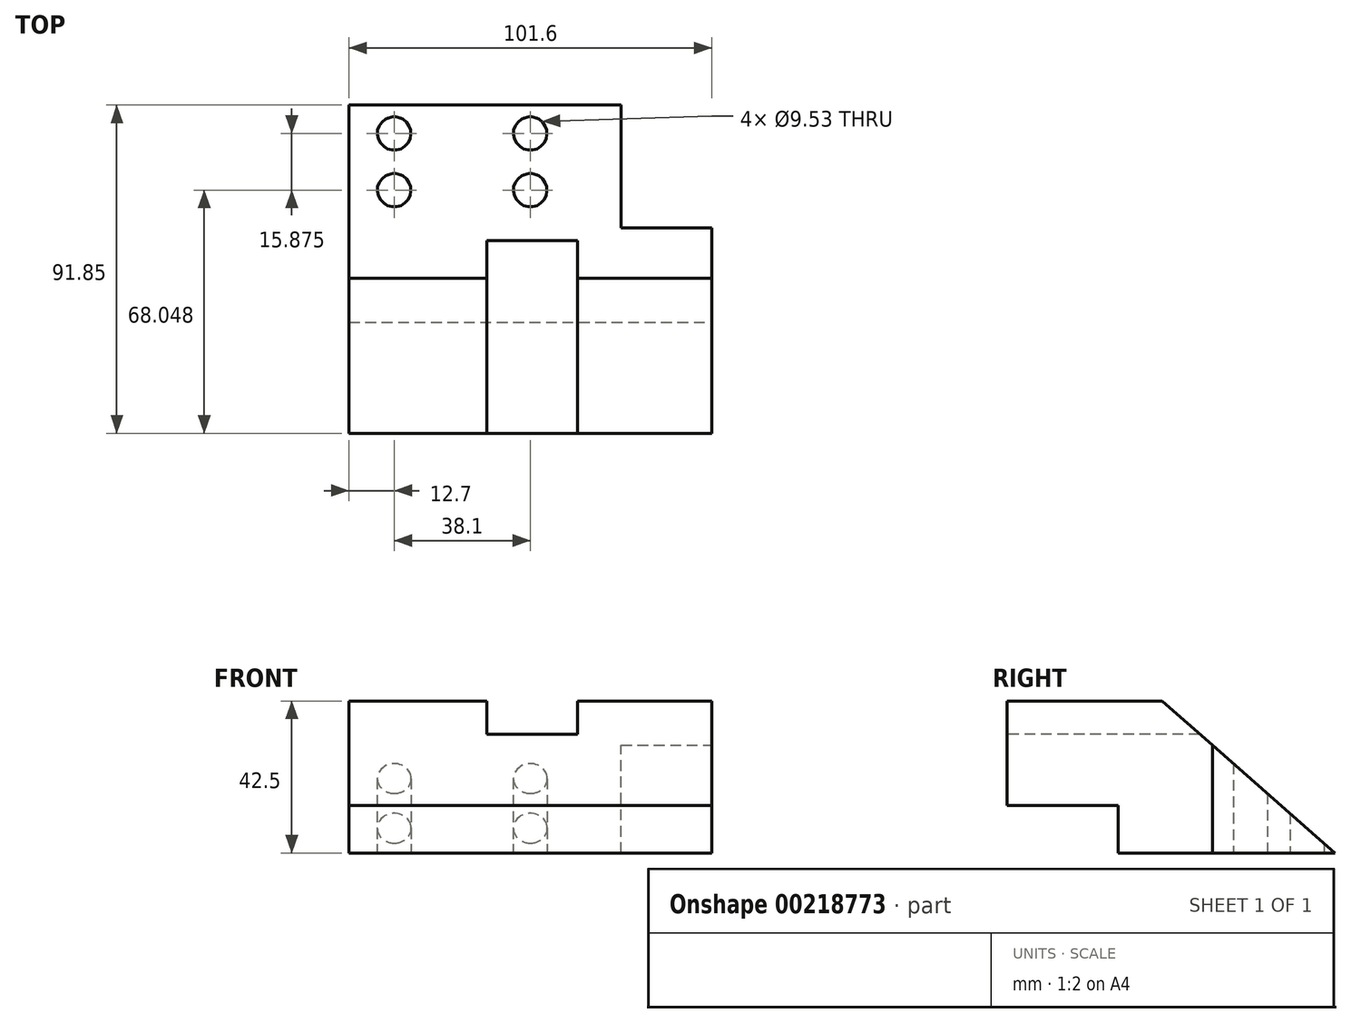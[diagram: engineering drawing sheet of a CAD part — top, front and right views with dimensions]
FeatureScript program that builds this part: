
annotation { "Feature Type Name" : "Feature", "Feature Type Description" : "" }
export const myFeature = defineFeature(function(context is Context, id is Id, definition is map)
    precondition{}
    {
        {
            var Q0;
            Q0=qCreatedBy(makeId("Right.planeOp"),FACE);
            var sketch = newSketch(context, id + "F0", { "sketchPlane" : qUnion([Q0])});
            skLineSegment(sketch, "E0", {"start": v(0, 0) * mm, "end": v(0, 29.24) * mm});
            skLineSegment(sketch, "E1", {"start": v(0, 29.24) * mm, "end": v(43.36, 29.24) * mm});
            skLineSegment(sketch, "E2", {"start": v(43.36, 29.24) * mm, "end": v(91.85, -13.26) * mm});
            skLineSegment(sketch, "E3", {"start": v(91.85, -13.26) * mm, "end": v(31.1, -13.26) * mm});
            skLineSegment(sketch, "E4", {"start": v(31.1, -13.26) * mm, "end": v(31.1, 0) * mm});
            skLineSegment(sketch, "E5", {"start": v(31.1, 0) * mm, "end": v(0, 0) * mm});
            skSolve(sketch);
        }
        {
            var Q0;
            Q0 = qSketchRegion(id + "F0", true);
            extrude(context, id + "F1", {"entities" : qUnion([Q0]), "endBound" : BoundingType.SYMMETRIC, "oppositeDirection" : true, "depth" : 101.6 * mm});
        }
        {
            var Q0;
            Q0=makeQuery(id+"F1.opExtrude","SWEPT_FACE",FACE,{"disambiguationData":[OSD([sQuery(id+"F0.wireOp",EDGE,"E0")])]});
            var sketch = newSketch(context, id + "F2", { "sketchPlane" : qUnion([Q0])});
            skLineSegment(sketch, "E6", {"start": v(0, 29.24) * mm, "end": v(-12.24, 29.24) * mm});
            skLineSegment(sketch, "E7", {"start": v(-12.24, 29.24) * mm, "end": v(-12.24, 20.03) * mm});
            skLineSegment(sketch, "E8", {"start": v(-12.24, 20.03) * mm, "end": v(13.16, 20.03) * mm});
            skLineSegment(sketch, "E9", {"start": v(13.16, 20.03) * mm, "end": v(13.16, 29.24) * mm});
            skLineSegment(sketch, "E10", {"start": v(13.16, 29.24) * mm, "end": v(0, 29.24) * mm});
            skSolve(sketch);
        }
        {
            var Q0;
            Q0=makeQuery(id+"F2.imprint","IMPRINT",FACE,{"disambiguationData":[TD([[makeQuery(id+"F2.imprint","IMPRINT",EDGE,{"derivedFrom":sQuery(id+"F2.wireOp",EDGE,"E6")}),-1.0]])]});
            extrude(context, id + "F3", {"entities" : qUnion([Q0]), "operationType" : NewBodyOperationType.REMOVE, "endBound" : BoundingType.UP_TO_NEXT, "oppositeDirection" : true, "depth" : 25.4 * mm});
        }
        {
            var Q0;
            Q0=makeQuery(id+"F1.opExtrude","CAP_FACE",FACE,{"disambiguationData":[OSD([sQuery(id+"F0.wireOp",EDGE,"E0"),sQuery(id+"F0.wireOp",EDGE,"E1"),sQuery(id+"F0.wireOp",EDGE,"E2"),sQuery(id+"F0.wireOp",EDGE,"E3"),sQuery(id+"F0.wireOp",EDGE,"E4"),sQuery(id+"F0.wireOp",EDGE,"E5")])],"isStart":true});
            var sketch = newSketch(context, id + "F4", { "sketchPlane" : qUnion([Q0])});
            skLineSegment(sketch, "E11", {"start": v(91.85, -13.26) * mm, "end": v(57.46, -13.26) * mm});
            skLineSegment(sketch, "E12", {"start": v(57.46, -13.26) * mm, "end": v(57.46, 30.38) * mm});
            skLineSegment(sketch, "E13", {"start": v(57.46, 30.38) * mm, "end": v(91.85, 30.38) * mm});
            skLineSegment(sketch, "E14", {"start": v(91.85, 30.38) * mm, "end": v(91.85, -13.26) * mm});
            skSolve(sketch);
        }
        {
            var Q0;
            Q0 = qSketchRegion(id + "F4", true);
            extrude(context, id + "F5", {"entities" : qUnion([Q0]), "operationType" : NewBodyOperationType.REMOVE, "oppositeDirection" : true, "depth" : 25.4 * mm});
        }
        {
            var Q0;
            Q0=qCreatedBy(makeId("Top.planeOp"),FACE);
            var sketch = newSketch(context, id + "F6", { "sketchPlane" : qUnion([Q0])});
            skCircle(sketch, "E15", {"center": v(-38.1, 83.92) * mm, "radius": 4.76 * mm});
            skCircle(sketch, "E16", {"center": v(-38.1, 68.05) * mm, "radius": 4.76 * mm});
            skCircle(sketch, "E17", {"center": v(0, 83.92) * mm, "radius": 4.76 * mm});
            skCircle(sketch, "E18", {"center": v(0, 68.05) * mm, "radius": 4.76 * mm});
            skSolve(sketch);
        }
        {
            var Q0;
            Q0 = qSketchRegion(id + "F6", true);
            extrude(context, id + "F7", {"entities" : qUnion([Q0]), "operationType" : NewBodyOperationType.REMOVE, "endBound" : BoundingType.SYMMETRIC, "depth" : 101.6 * mm});
        }
    });
